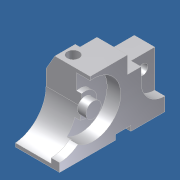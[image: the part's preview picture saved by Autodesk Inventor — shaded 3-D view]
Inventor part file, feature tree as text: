
AUTODESK INVENTOR PART (.ipt)
format: ipt  version: unknown  size: 333,312 bytes
history: native  units: in
note: dims shown in document units (in); Inventor stores cm internally (conversion verified against a paired STEP export)
features: sketch x14, extrude x12, projected_geometry x3, hole x2
ambient origin geometry x8: Origin, YZ Plane, XZ Plane, XY Plane, X Axis, Y Axis, Z Axis, Center Point
bodies: Solid1 (feature_tree)
feature tree (31):
  extrude  "Extrusion1"  Depth=2.5in
  extrude  "Extrusion2"  Depth=1.25in
  extrude  "Extrusion3"  Depth=0.562in
  extrude  "Extrusion4"  Depth=1.25in
  extrude  "Extrusion5"  Depth=2.0in
  extrude  "Extrusion6"  Depth=0.5in TaperAngle=0.0deg
  extrude  "Extrusion7"  Depth=0.3125in TaperAngle=0.0deg
  extrude  "Extrusion8"  Depth=0.125in
  extrude  "Extrusion9"  Depth=1.3125in TaperAngle=0.0deg
  hole  "Hole1"  [1 undecoded]
  hole  "Hole2"  [1 undecoded]
  extrude  "Extrusion10"  Depth=1.3125in TaperAngle=0.0deg
  extrude  "Extrusion11"  Depth=0.375in TaperAngle=0.0deg
  extrude  "Extrusion12"  Depth=0.625in
  sketch  "Sketch1"  dims[d0=3.875in d1=2.5in]
  sketch  "Sketch2"  dims[d2=1.625in d3=0.0in d4=1.25in]
  sketch  "Sketch3"  dims[d5=0.1875in d6=0.562in]
  sketch  "Sketch4"  dims[d7=1.625in d8=0.0in d9=1.25in]
  sketch  "Sketch5"  dims[d10=1.375in d11=2.0in]
  sketch  "Sketch6"  dims[d12=0.876in d13=0.5in d14=0.0in]
  sketch  "Sketch7"  dims[d15=0.562in d16=0.3125in d17=0.0in]
  projected_geometry  "Projected Loop1"
  sketch  "Sketch8"  dims[d18=1.375in d19=0.125in]
  sketch  "Sketch9"  dims[d20=2.5in d21=1.3125in d22=0.0in]
  sketch  "Sketch10"  dims[d23=2.125in d24=1.3125in d25=0.0in]
  sketch  "Sketch11"  dims[d26=1.3125in d27=0.0in d28=1.375in]
  sketch  "Sketch12"  dims[d29=0.625in d30=1.3125in d31=0.0in]
  projected_geometry  "Projected Loop2"
  sketch  "Sketch13"  dims[d32=1.75in d33=0.375in d34=0.0in]
  projected_geometry  "Projected Loop3"
  sketch  "Sketch14"  dims[d35=0.4375in d36=0.375in d37=0.75in d38=0.375in d39=0.25in d40=0.5635in d41=1.0in d42=0.8108in d43=0.625in d44=0.375in d45=0.4375in d46=0.75in d47=0.375in d48=0.25in d49=0.5635in d50=1.0in d51=0.8108in d52=0.5in d53=2.0in d54=0.375in d55=0.0in d56=0.5in d57=2.0in d58=0.375in d59=0.0in d60=0.5625in d61=30.0deg d62=0.375in d63=0.0in]
note: 2 required parameter values undecoded (feature->parameter linkage not recoverable at this tier; creation-order binding heuristic only, values carry confidence <= 0.55)
